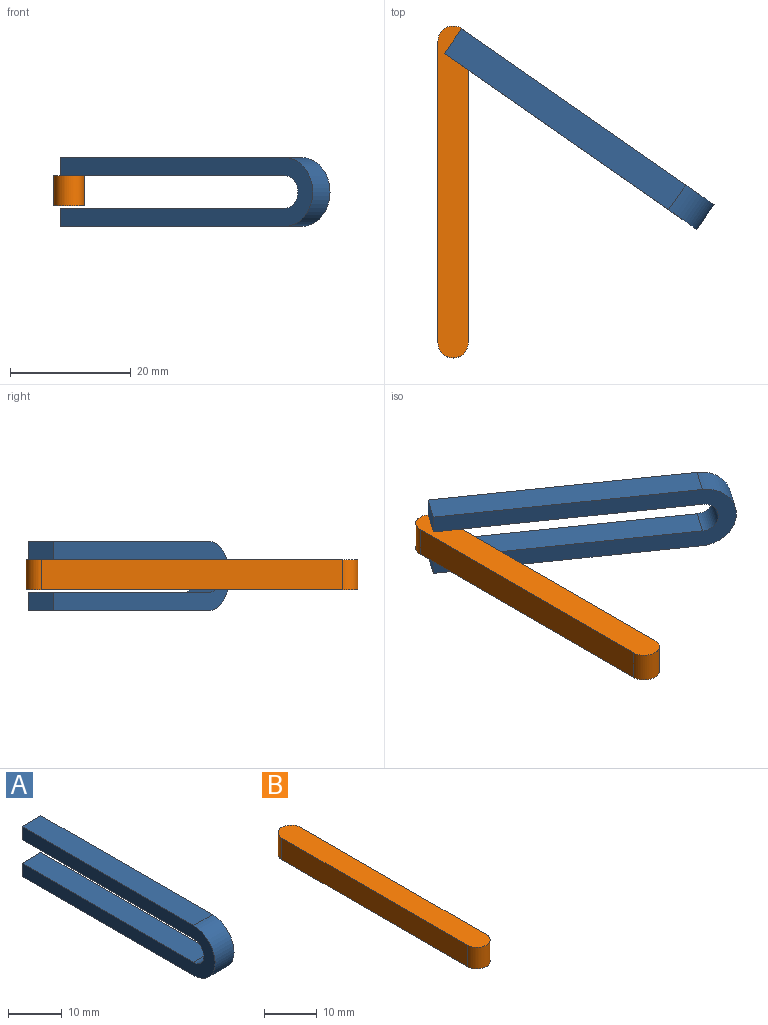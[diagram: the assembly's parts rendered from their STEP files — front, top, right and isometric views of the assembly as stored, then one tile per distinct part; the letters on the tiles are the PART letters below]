
ASSEMBLY  parts=2 mates=1
PART A: 10 faces, bbox 5x51x11.4 mm
  f0: plane 45.26x5mm, normal (0,0,-1), area 226.3mm2, adj f1,f7,f8,f9
  f1: plane 5x3mm, normal (0,1,0), area 15mm2, adj f0,f2,f8,f9
  f2: plane 45.26x5mm, normal (0,0,1), area 226.3mm2, adj f1,f3,f8,f9
  f3: cylinder r=5.7mm len=11.4mm, axis (-1,0,0), area 89.5mm2, adj f2,f4,f8,f9
  f4: plane 45.26x5mm, normal (0,0,-1), area 226.3mm2, adj f3,f5,f8,f9
  f5: plane 5x3mm, normal (0,1,0), area 15mm2, adj f4,f6,f8,f9
  f6: plane 45.26x5mm, normal (0,0,1), area 226.3mm2, adj f5,f7,f8,f9
  f7: cylinder r=2.7mm len=5.4mm, axis (-1,0,0), area 42.4mm2, adj f0,f6,f8,f9
  f8: plane 50.96x11.4mm, normal (1,0,0), area 311.2mm2, adj f0,f1,f2,f3,f4,f5,f6,f7
  f9: plane 50.96x11.4mm, normal (-1,0,0), area 311.2mm2, adj f0,f1,f2,f3,f4,f5,f6,f7
PART B: 6 faces, bbox 5x55x5 mm
  f0: plane 50x5mm, normal (-1,0,0), area 250mm2, adj f1,f3,f4,f5
  f1: cylinder r=2.5mm len=5mm, axis (0,0,-1), area 39.3mm2, adj f0,f2,f4,f5
  f2: plane 50x5mm, normal (1,0,0), area 250mm2, adj f1,f3,f4,f5
  f3: cylinder r=2.5mm len=5mm, axis (0,0,-1), area 39.3mm2, adj f0,f2,f4,f5
  f4: plane 55x5mm, normal (0,0,1), area 269.6mm2, adj f0,f1,f2,f3
  f5: plane 55x5mm, normal (0,0,-1), area 269.6mm2, adj f0,f1,f2,f3
PLACE A rot(axis=(0,0,1),55.1deg) t=(21.13,7.22,2.3)mm
PLACE B t=(0,0,2.5)mm
MATE revolute B.f3 <-> A.f0  axis (0,0,1) through (0,25,5)mm
